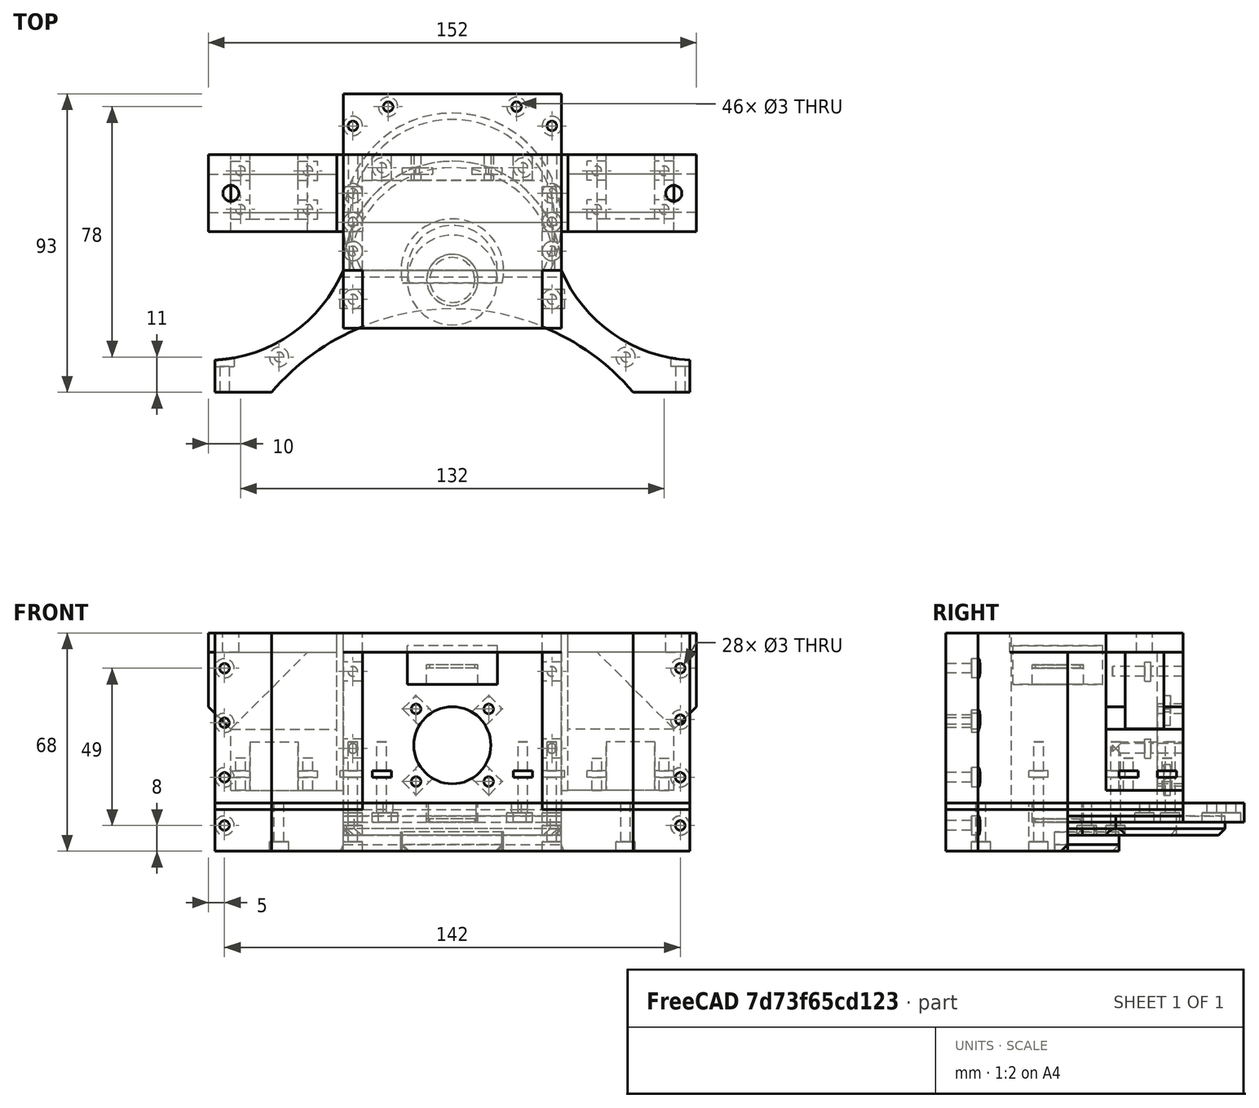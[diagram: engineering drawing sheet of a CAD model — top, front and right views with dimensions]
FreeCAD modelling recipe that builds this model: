
FCSTD DOCUMENT  (FreeCAD 0.19R24291 (Git))
Label: bazovina-part-J_rear-gearbox-cover_013
License: All rights reserved
LicenseURL: http://en.wikipedia.org/wiki/All_rights_reserved
objects: Part::Cylinder×179, Part::Cut×89, Part::Compound×79, Part::Box×59, Part::Chamfer×18, Mesh::Feature×2, Part::FeaturePython×2, Part::Mirroring×1
note: 427 computed .brp shape members not serialized (recipe doc carries the construction recipe); baked Part::Feature solids carry a one-line shape summary decoded from their .brp

FEATURE [Part::Cylinder] Cylinder483  label="Válec483"
  Angle = 360
  AttacherType = Attacher::AttachEngine3D
  Height = 36
  Placement = pos=(-76.3,104,16) rot=(0,0,1;0rad)
  Radius = 46
FEATURE [Part::Cylinder] Cylinder484  label="Válec484"
  Angle = 360
  AttacherType = Attacher::AttachEngine3D
  Height = 36
  Placement = pos=(76.3,104,16) rot=(0,0,1;0rad)
  Radius = 46
FEATURE [Part::Box] Box177  label="Krychle177"
  AttacherType = Attacher::AttachEngine3D
  Height = 15
  Length = 148
  Placement = pos=(-74,48,16) rot=(0,0,1;0rad)
  Width = 38
FEATURE [Part::Cut] Cut186
  Base = -> Box177
  Tool = -> Cylinder483
FEATURE [Part::Cut] Cut187
  Base = -> Cut186
  Tool = -> Cylinder484
FEATURE [Part::Cylinder] Cylinder486  label="Válec486"
  Angle = 360
  AttacherType = Attacher::AttachEngine3D
  Height = 15
  Placement = pos=(0,0,16) rot=(0,0,1;0rad)
  Radius = 74
FEATURE [Part::Cut] Cut189
  Base = -> Cut187
  Tool = -> Cylinder486
FEATURE [Part::Cylinder] Cylinder488  label="Válec488"
  Angle = 360
  AttacherType = Attacher::AttachEngine3D
  Height = 6
  Placement = pos=(0,86,21) rot=(0,0,1;0rad)
  Radius = 34
FEATURE [Part::Box] Box183  label="Krychle183"
  AttacherType = Attacher::AttachEngine3D
  Height = 40
  Length = 148
  Placement = pos=(-74,46,16) rot=(0,0,1;0rad)
  Width = 40
FEATURE [Part::Cut] Cut194
  Base = -> Cylinder488
  Tool = -> Box183
FEATURE [Part::Cylinder] Cylinder539  label="Válec539"
  Angle = 360
  AttacherType = Attacher::AttachEngine3D
  Height = 50
  Placement = pos=(71,80,24) rot=(1,0,0;1.5708rad)
  Radius = 1.5
FEATURE [Part::Cylinder] Cylinder540  label="Válec540"
  Angle = 360
  AttacherType = Attacher::AttachEngine3D
  Height = 50
  Placement = pos=(-71,80,24) rot=(1,0,0;1.5708rad)
  Radius = 1.5
FEATURE [Part::Compound] Compound348
  Links = -> [Cylinder539,Cylinder540]
FEATURE [Part::Cut] Cut209
  Base = -> Cut189
  Tool = -> Compound348
FEATURE [Part::Cylinder] Cylinder541  label="Válec541"
  Angle = 360
  AttacherType = Attacher::AttachEngine3D
  Height = 50
  Placement = pos=(-71,106,24) rot=(1,0,0;1.5708rad)
  Radius = 3
FEATURE [Part::Cylinder] Cylinder542  label="Válec542"
  Angle = 360
  AttacherType = Attacher::AttachEngine3D
  Height = 50
  Placement = pos=(71,106,24) rot=(1,0,0;1.5708rad)
  Radius = 3
FEATURE [Part::Compound] Compound349
  Links = -> [Cylinder542,Cylinder541]
FEATURE [Part::Cut] Cut210
  Base = -> Cut209
  Tool = -> Compound349
FEATURE [Part::Cylinder] Cylinder626  label="Válec626"
  Angle = 360
  AttacherType = Attacher::AttachEngine3D
  Height = 50
  Placement = pos=(-31,110,0) rot=(0,0,1;0.785398rad)
  Radius = 1.5
FEATURE [Part::Box] Box242  label="Krychle242"
  AttacherType = Attacher::AttachEngine3D
  Height = 4
  Length = 68
  Placement = pos=(-34,86,27) rot=(0,0,1;0rad)
  Width = 36
FEATURE [Part::Cylinder] Cylinder625  label="Válec625"
  Angle = 360
  AttacherType = Attacher::AttachEngine3D
  Height = 6
  Placement = pos=(0,86,16) rot=(0,0,1;0rad)
  Radius = 16
FEATURE [Part::Box] Box243  label="Krychle243"
  AttacherType = Attacher::AttachEngine3D
  Height = 40
  Length = 148
  Placement = pos=(-74,42,16) rot=(0,0,1;0rad)
  Width = 40
FEATURE [Part::Cut] Cut246
  Base = -> Cylinder625
  Tool = -> Box243
FEATURE [Part::Cylinder] Cylinder632  label="Válec632"
  Angle = 360
  AttacherType = Attacher::AttachEngine3D
  Height = 3
  Placement = pos=(31,110,0) rot=(0,0,1;0.785398rad)
  Radius = 3
FEATURE [Part::Cylinder] Cylinder633  label="Válec633"
  Angle = 360
  AttacherType = Attacher::AttachEngine3D
  Height = 3
  Placement = pos=(31,92,21) rot=(0,0,1;0.785398rad)
  Radius = 3
FEATURE [Part::Cylinder] Cylinder637  label="Válec637"
  Angle = 360
  AttacherType = Attacher::AttachEngine3D
  Height = 50
  Placement = pos=(-31,92,0) rot=(0,0,1;0.785398rad)
  Radius = 1.5
FEATURE [Part::Cylinder] Cylinder636  label="Válec636"
  Angle = 360
  AttacherType = Attacher::AttachEngine3D
  Height = 50
  Placement = pos=(31,110,0) rot=(0,0,1;0.785398rad)
  Radius = 1.5
FEATURE [Part::Cylinder] Cylinder634  label="Válec634"
  Angle = 360
  AttacherType = Attacher::AttachEngine3D
  Height = 50
  Placement = pos=(-31,110,0) rot=(0,0,1;0.785398rad)
  Radius = 1.5
FEATURE [Part::Cylinder] Cylinder631  label="Válec631"
  Angle = 360
  AttacherType = Attacher::AttachEngine3D
  Height = 3
  Placement = pos=(-31,92,21) rot=(0,0,1;0.785398rad)
  Radius = 3
FEATURE [Part::Cylinder] Cylinder640  label="Válec640"
  Angle = 360
  AttacherType = Attacher::AttachEngine3D
  Height = 6
  Placement = pos=(0,83,25) rot=(0,0,1;0rad)
  Radius = 8
FEATURE [Part::Cylinder] Cylinder638  label="Válec638"
  Angle = 360
  AttacherType = Attacher::AttachEngine3D
  Height = 6
  Placement = pos=(0,83,25) rot=(0,0,1;0rad)
  Radius = 8
FEATURE [Part::Cylinder] Cylinder629  label="Válec629"
  Angle = 360
  AttacherType = Attacher::AttachEngine3D
  Height = 50
  Placement = pos=(31,92,0) rot=(0,0,1;0.785398rad)
  Radius = 1.5
FEATURE [Part::Cylinder] Cylinder630  label="Válec630"
  Angle = 360
  AttacherType = Attacher::AttachEngine3D
  Height = 3
  Placement = pos=(-31,110,0) rot=(0,0,1;0.785398rad)
  Radius = 3
FEATURE [Part::Cylinder] Cylinder628  label="Válec628"
  Angle = 360
  AttacherType = Attacher::AttachEngine3D
  Height = 50
  Placement = pos=(31,110,0) rot=(0,0,1;0.785398rad)
  Radius = 1.5
FEATURE [Part::Cylinder] Cylinder627  label="Válec627"
  Angle = 360
  AttacherType = Attacher::AttachEngine3D
  Height = 50
  Placement = pos=(-31,92,0) rot=(0,0,1;0.785398rad)
  Radius = 1.5
FEATURE [Part::Compound] Compound385
  Links = -> [Cylinder626,Cylinder627,Cylinder628,Cylinder629]
FEATURE [Part::Cut] Cut248
  Base = -> Cut194
  Tool = -> Compound385
FEATURE [Part::Cylinder] Cylinder635  label="Válec635"
  Angle = 360
  AttacherType = Attacher::AttachEngine3D
  Height = 50
  Placement = pos=(31,92,0) rot=(0,0,1;0.785398rad)
  Radius = 1.5
FEATURE [Part::Cylinder] Cylinder639  label="Válec639"
  Angle = 360
  AttacherType = Attacher::AttachEngine3D
  Height = 6
  Placement = pos=(0,83,25) rot=(0,0,1;0rad)
  Radius = 8
FEATURE [Part::Compound] Compound386
  Links = -> [Cylinder634,Cylinder637,Cylinder636,Cylinder635]
FEATURE [Part::Cut] Cut247
  Base = -> Box242
  Tool = -> Compound386
FEATURE [Part::Cut] Cut250
  Base = -> Cut247
  Tool = -> Cylinder638
FEATURE [Part::Cut] Cut252
  Base = -> Cut210
  Tool = -> Cylinder640
FEATURE [Part::Compound] Compound387
  Links = -> [Cylinder630,Cylinder631,Cylinder632,Cylinder633]
FEATURE [Part::Cut] Cut249
  Base = -> Cut248
  Tool = -> Compound387
FEATURE [Part::Cut] Cut251
  Base = -> Cut249
  Tool = -> Cylinder639
FEATURE [Part::Compound] Compound388  label="bazovina-part-J"
  Links = -> [Cut252,Cut250,Cut251,Cut246]
FEATURE [Part::Box] Box244  label="Krychle244"
  AttacherType = Attacher::AttachEngine3D
  Height = 40
  Length = 148
  Placement = pos=(-74,46,16) rot=(0,0,1;0rad)
  Width = 40
FEATURE [Part::Cylinder] Cylinder641  label="Válec641"
  Angle = 360
  AttacherType = Attacher::AttachEngine3D
  Height = 3
  Placement = pos=(31,92,21) rot=(0,0,1;0.785398rad)
  Radius = 3
FEATURE [Part::Cylinder] Cylinder642  label="Válec642"
  Angle = 360
  AttacherType = Attacher::AttachEngine3D
  Height = 36
  Placement = pos=(-76.3,104,16) rot=(0,0,1;0rad)
  Radius = 46
FEATURE [Part::Cylinder] Cylinder643  label="Válec643"
  Angle = 360
  AttacherType = Attacher::AttachEngine3D
  Height = 36
  Placement = pos=(76.3,104,16) rot=(0,0,1;0rad)
  Radius = 46
FEATURE [Part::Box] Box245  label="Krychle245"
  AttacherType = Attacher::AttachEngine3D
  Height = 15
  Length = 148
  Placement = pos=(-74,48,16) rot=(0,0,1;0rad)
  Width = 38
FEATURE [Part::Cylinder] Cylinder644  label="Válec644"
  Angle = 360
  AttacherType = Attacher::AttachEngine3D
  Height = 50
  Placement = pos=(-71,80,24) rot=(1,0,0;1.5708rad)
  Radius = 1.5
FEATURE [Part::Cylinder] Cylinder645  label="Válec645"
  Angle = 360
  AttacherType = Attacher::AttachEngine3D
  Height = 50
  Placement = pos=(-31,110,0) rot=(0,0,1;0.785398rad)
  Radius = 1.5
FEATURE [Part::Cylinder] Cylinder646  label="Válec646"
  Angle = 360
  AttacherType = Attacher::AttachEngine3D
  Height = 15
  Placement = pos=(0,0,16) rot=(0,0,1;0rad)
  Radius = 74
FEATURE [Part::Cylinder] Cylinder647  label="Válec647"
  Angle = 360
  AttacherType = Attacher::AttachEngine3D
  Height = 6
  Placement = pos=(0,86,21) rot=(0,0,1;0rad)
  Radius = 34
FEATURE [Part::Cylinder] Cylinder648  label="Válec648"
  Angle = 360
  AttacherType = Attacher::AttachEngine3D
  Height = 50
  Placement = pos=(-71,106,24) rot=(1,0,0;1.5708rad)
  Radius = 3
FEATURE [Part::Box] Box246  label="Krychle246"
  AttacherType = Attacher::AttachEngine3D
  Height = 4
  Length = 68
  Placement = pos=(-34,86,27) rot=(0,0,1;0rad)
  Width = 36
FEATURE [Part::Box] Box247  label="Krychle247"
  AttacherType = Attacher::AttachEngine3D
  Height = 40
  Length = 148
  Placement = pos=(-74,42,16) rot=(0,0,1;0rad)
  Width = 40
FEATURE [Part::Cylinder] Cylinder649  label="Válec649"
  Angle = 360
  AttacherType = Attacher::AttachEngine3D
  Height = 50
  Placement = pos=(71,80,24) rot=(1,0,0;1.5708rad)
  Radius = 1.5
FEATURE [Part::Compound] Compound390
  Links = -> [Cylinder649,Cylinder644]
FEATURE [Part::Cylinder] Cylinder650  label="Válec650"
  Angle = 360
  AttacherType = Attacher::AttachEngine3D
  Height = 6
  Placement = pos=(0,86,16) rot=(0,0,1;0rad)
  Radius = 16
FEATURE [Part::Cylinder] Cylinder651  label="Válec651"
  Angle = 360
  AttacherType = Attacher::AttachEngine3D
  Height = 50
  Placement = pos=(71,106,24) rot=(1,0,0;1.5708rad)
  Radius = 3
FEATURE [Part::Compound] Compound391
  Links = -> [Cylinder651,Cylinder648]
FEATURE [Part::Cylinder] Cylinder652  label="Válec652"
  Angle = 360
  AttacherType = Attacher::AttachEngine3D
  Height = 3
  Placement = pos=(31,110,0) rot=(0,0,1;0.785398rad)
  Radius = 3
FEATURE [Part::Cylinder] Cylinder653  label="Válec653"
  Angle = 360
  AttacherType = Attacher::AttachEngine3D
  Height = 50
  Placement = pos=(31,110,0) rot=(0,0,1;0.785398rad)
  Radius = 1.5
FEATURE [Part::Cylinder] Cylinder654  label="Válec654"
  Angle = 360
  AttacherType = Attacher::AttachEngine3D
  Height = 50
  Placement = pos=(-31,110,0) rot=(0,0,1;0.785398rad)
  Radius = 1.5
FEATURE [Part::Cylinder] Cylinder655  label="Válec655"
  Angle = 360
  AttacherType = Attacher::AttachEngine3D
  Height = 3
  Placement = pos=(-31,92,21) rot=(0,0,1;0.785398rad)
  Radius = 3
FEATURE [Part::Cylinder] Cylinder656  label="Válec656"
  Angle = 360
  AttacherType = Attacher::AttachEngine3D
  Height = 50
  Placement = pos=(-31,92,0) rot=(0,0,1;0.785398rad)
  Radius = 1.5
FEATURE [Part::Cylinder] Cylinder657  label="Válec657"
  Angle = 360
  AttacherType = Attacher::AttachEngine3D
  Height = 6
  Placement = pos=(0,83,25) rot=(0,0,1;0rad)
  Radius = 8
FEATURE [Part::Cylinder] Cylinder658  label="Válec658"
  Angle = 360
  AttacherType = Attacher::AttachEngine3D
  Height = 50
  Placement = pos=(31,92,0) rot=(0,0,1;0.785398rad)
  Radius = 1.5
FEATURE [Part::Cylinder] Cylinder659  label="Válec659"
  Angle = 360
  AttacherType = Attacher::AttachEngine3D
  Height = 6
  Placement = pos=(0,83,25) rot=(0,0,1;0rad)
  Radius = 8
FEATURE [Part::Cylinder] Cylinder660  label="Válec660"
  Angle = 360
  AttacherType = Attacher::AttachEngine3D
  Height = 3
  Placement = pos=(-31,110,0) rot=(0,0,1;0.785398rad)
  Radius = 3
FEATURE [Part::Compound] Compound394
  Links = -> [Cylinder660,Cylinder655,Cylinder652,Cylinder641]
FEATURE [Part::Cylinder] Cylinder661  label="Válec661"
  Angle = 360
  AttacherType = Attacher::AttachEngine3D
  Height = 50
  Placement = pos=(31,110,0) rot=(0,0,1;0.785398rad)
  Radius = 1.5
FEATURE [Part::Cylinder] Cylinder662  label="Válec662"
  Angle = 360
  AttacherType = Attacher::AttachEngine3D
  Height = 50
  Placement = pos=(-31,92,0) rot=(0,0,1;0.785398rad)
  Radius = 1.5
FEATURE [Part::Compound] Compound392
  Links = -> [Cylinder645,Cylinder662,Cylinder661,Cylinder658]
FEATURE [Part::Cylinder] Cylinder663  label="Válec663"
  Angle = 360
  AttacherType = Attacher::AttachEngine3D
  Height = 6
  Placement = pos=(0,83,25) rot=(0,0,1;0rad)
  Radius = 8
FEATURE [Part::Cylinder] Cylinder664  label="Válec664"
  Angle = 360
  AttacherType = Attacher::AttachEngine3D
  Height = 50
  Placement = pos=(31,92,0) rot=(0,0,1;0.785398rad)
  Radius = 1.5
FEATURE [Part::Compound] Compound393
  Links = -> [Cylinder654,Cylinder656,Cylinder653,Cylinder664]
FEATURE [Part::Cut] Cut255
  Base = -> Box245
  Tool = -> Cylinder642
FEATURE [Part::Cut] Cut256
  Base = -> Cylinder647
  Tool = -> Box244
FEATURE [Part::Cut] Cut259
  Base = -> Box246
  Tool = -> Compound393
FEATURE [Part::Cut] Cut260
  Base = -> Cut259
  Tool = -> Cylinder659
FEATURE [Part::Cut] Cut262
  Base = -> Cylinder650
  Tool = -> Box247
FEATURE [Part::Cut] Cut263
  Base = -> Cut255
  Tool = -> Cylinder643
FEATURE [Part::Cut] Cut261
  Base = -> Cut263
  Tool = -> Cylinder646
FEATURE [Part::Cut] Cut253
  Base = -> Cut261
  Tool = -> Compound390
FEATURE [Part::Cut] Cut264
  Base = -> Cut253
  Tool = -> Compound391
FEATURE [Part::Cut] Cut254
  Base = -> Cut264
  Tool = -> Cylinder657
FEATURE [Part::Cut] Cut265
  Base = -> Cut256
  Tool = -> Compound392
FEATURE [Part::Cut] Cut258
  Base = -> Cut265
  Tool = -> Compound394
FEATURE [Part::Cut] Cut257
  Base = -> Cut258
  Tool = -> Cylinder663
FEATURE [Part::Compound] Compound389  label="bazovina-part-J001"
  Links = -> [Cut254,Cut260,Cut257,Cut262]
FEATURE [Part::Chamfer] Chamfer
  Base = -> Compound389
  Edges = 1 edges r=2: [Edge24]
FEATURE [Part::Chamfer] Chamfer001
  Base = -> Chamfer
  Edges = 1 edges r=2: [Edge94]
FEATURE [Part::Chamfer] Chamfer002
  Base = -> Chamfer001
  Edges = 1 edges r=2: [Edge4]
FEATURE [Part::Chamfer] Chamfer003  label="bazovina-part-J_fino"
  Base = -> Chamfer002
  Edges = 1 edges r=2: [Edge6]
FEATURE [Part::Chamfer] Chamfer004  label="bazovina-part-J_fino001"
  Base = -> Chamfer003
  Edges = 1 edges r=2: [Edge136]
FEATURE [Mesh::Feature] Mesh  label="bazovina-part-J_fino001 (Meshed)"
FEATURE [Part::FeaturePython] Tube032  # WARN: FeaturePython — macro-defined, semantics opaque (R4)
  AttacherType = Attacher::AttachEngine3D
  Height = 1
  InnerRadius = 7
  OuterRadius = 8
  Placement = pos=(0,83,25) rot=(0,0,1;0rad)
FEATURE [Part::Cylinder] Cylinder665  label="Válec665"
  Angle = 360
  AttacherType = Attacher::AttachEngine3D
  Height = 36
  Placement = pos=(76.3,104,16) rot=(0,0,1;0rad)
  Radius = 46
FEATURE [Part::Cylinder] Cylinder666  label="Válec666"
  Angle = 360
  AttacherType = Attacher::AttachEngine3D
  Height = 36
  Placement = pos=(-76.3,104,16) rot=(0,0,1;0rad)
  Radius = 46
FEATURE [Part::Box] Box248  label="Krychle248"
  AttacherType = Attacher::AttachEngine3D
  Height = 15
  Length = 148
  Placement = pos=(-74,48,16) rot=(0,0,1;0rad)
  Width = 38
FEATURE [Part::Cut] Cut269
  Base = -> Box248
  Tool = -> Cylinder666
FEATURE [Part::Cut] Cut270
  Base = -> Cut269
  Tool = -> Cylinder665
FEATURE [Part::Cylinder] Cylinder667  label="Válec667"
  Angle = 360
  AttacherType = Attacher::AttachEngine3D
  Height = 15
  Placement = pos=(0,0,16) rot=(0,0,1;0rad)
  Radius = 74
FEATURE [Part::Cut] Cut267
  Base = -> Cut270
  Tool = -> Cylinder667
FEATURE [Part::Box] Box249  label="Krychle249"
  AttacherType = Attacher::AttachEngine3D
  Height = 6
  Length = 68
  Placement = pos=(-34,86,25) rot=(0,0,1;0rad)
  Width = 36
FEATURE [Part::Box] Box250  label="Krychle250"
  AttacherType = Attacher::AttachEngine3D
  Height = 40
  Length = 148
  Placement = pos=(-74,46,16) rot=(0,0,1;0rad)
  Width = 40
FEATURE [Part::Box] Box251  label="Krychle251"
  AttacherType = Attacher::AttachEngine3D
  Height = 40
  Length = 148
  Placement = pos=(-74,42,16) rot=(0,0,1;0rad)
  Width = 40
FEATURE [Part::Cylinder] Cylinder668  label="Válec668"
  Angle = 360
  AttacherType = Attacher::AttachEngine3D
  Height = 3
  Placement = pos=(31,110,0) rot=(0,0,1;0.785398rad)
  Radius = 3
FEATURE [Part::Cylinder] Cylinder669  label="Válec669"
  Angle = 360
  AttacherType = Attacher::AttachEngine3D
  Height = 50
  Placement = pos=(-31,92,0) rot=(0,0,1;0.785398rad)
  Radius = 1.5
FEATURE [Part::Cylinder] Cylinder670  label="Válec670"
  Angle = 360
  AttacherType = Attacher::AttachEngine3D
  Height = 50
  Placement = pos=(-71,80,24) rot=(1,0,0;1.5708rad)
  Radius = 1.5
FEATURE [Part::Cylinder] Cylinder671  label="Válec671"
  Angle = 360
  AttacherType = Attacher::AttachEngine3D
  Height = 6
  Placement = pos=(0,86,21) rot=(0,0,1;0rad)
  Radius = 34
FEATURE [Part::Cylinder] Cylinder672  label="Válec672"
  Angle = 360
  AttacherType = Attacher::AttachEngine3D
  Height = 50
  Placement = pos=(31,110,0) rot=(0,0,1;0.785398rad)
  Radius = 1.5
FEATURE [Part::Cylinder] Cylinder673  label="Válec673"
  Angle = 360
  AttacherType = Attacher::AttachEngine3D
  Height = 50
  Placement = pos=(-31,110,0) rot=(0,0,1;0.785398rad)
  Radius = 1.5
FEATURE [Part::Cylinder] Cylinder674  label="Válec674"
  Angle = 360
  AttacherType = Attacher::AttachEngine3D
  Height = 6
  Placement = pos=(0,86,16) rot=(0,0,1;0rad)
  Radius = 16
FEATURE [Part::Cut] Cut268
  Base = -> Cylinder674
  Tool = -> Box251
FEATURE [Part::Cylinder] Cylinder675  label="Válec675"
  Angle = 360
  AttacherType = Attacher::AttachEngine3D
  Height = 50
  Placement = pos=(-31,110,0) rot=(0,0,1;0.785398rad)
  Radius = 1.5
FEATURE [Part::Cylinder] Cylinder676  label="Válec676"
  Angle = 360
  AttacherType = Attacher::AttachEngine3D
  Height = 3
  Placement = pos=(31,92,21) rot=(0,0,1;0.785398rad)
  Radius = 3
FEATURE [Part::Cylinder] Cylinder677  label="Válec677"
  Angle = 360
  AttacherType = Attacher::AttachEngine3D
  Height = 50
  Placement = pos=(-71,106,24) rot=(1,0,0;1.5708rad)
  Radius = 3
FEATURE [Part::Cylinder] Cylinder678  label="Válec678"
  Angle = 360
  AttacherType = Attacher::AttachEngine3D
  Height = 50
  Placement = pos=(71,106,24) rot=(1,0,0;1.5708rad)
  Radius = 3
FEATURE [Part::Compound] Compound398
  Links = -> [Cylinder678,Cylinder677]
FEATURE [Part::Cylinder] Cylinder679  label="Válec679"
  Angle = 360
  AttacherType = Attacher::AttachEngine3D
  Height = 50
  Placement = pos=(71,80,24) rot=(1,0,0;1.5708rad)
  Radius = 1.5
FEATURE [Part::Compound] Compound395
  Links = -> [Cylinder679,Cylinder670]
FEATURE [Part::Cut] Cut271
  Base = -> Cylinder671
  Tool = -> Box250
FEATURE [Part::Cut] Cut272
  Base = -> Cut267
  Tool = -> Compound395
FEATURE [Part::Cut] Cut273
  Base = -> Cut272
  Tool = -> Compound398
FEATURE [Part::Cylinder] Cylinder680  label="Válec680"
  Angle = 360
  AttacherType = Attacher::AttachEngine3D
  Height = 50
  Placement = pos=(31,92,0) rot=(0,0,1;0.785398rad)
  Radius = 1.5
FEATURE [Part::Compound] Compound397
  Links = -> [Cylinder673,Cylinder669,Cylinder672,Cylinder680]
FEATURE [Part::Cut] Cut276
  Base = -> Box249
  Tool = -> Compound397
FEATURE [Part::Cylinder] Cylinder681  label="Válec681"
  Angle = 360
  AttacherType = Attacher::AttachEngine3D
  Height = 50
  Placement = pos=(-31,92,0) rot=(0,0,1;0.785398rad)
  Radius = 1.5
FEATURE [Part::Cylinder] Cylinder682  label="Válec682"
  Angle = 360
  AttacherType = Attacher::AttachEngine3D
  Height = 6
  Placement = pos=(0,83,25) rot=(0,0,1;0rad)
  Radius = 8
FEATURE [Part::Cut] Cut266
  Base = -> Cut276
  Tool = -> Cylinder682
FEATURE [Part::Cylinder] Cylinder683  label="Válec683"
  Angle = 360
  AttacherType = Attacher::AttachEngine3D
  Height = 3
  Placement = pos=(-31,110,0) rot=(0,0,1;0.785398rad)
  Radius = 3
FEATURE [Part::Cylinder] Cylinder684  label="Válec684"
  Angle = 360
  AttacherType = Attacher::AttachEngine3D
  Height = 6
  Placement = pos=(0,83,25) rot=(0,0,1;0rad)
  Radius = 8
FEATURE [Part::Cylinder] Cylinder685  label="Válec685"
  Angle = 360
  AttacherType = Attacher::AttachEngine3D
  Height = 50
  Placement = pos=(31,92,0) rot=(0,0,1;0.785398rad)
  Radius = 1.5
FEATURE [Part::Cylinder] Cylinder686  label="Válec686"
  Angle = 360
  AttacherType = Attacher::AttachEngine3D
  Height = 50
  Placement = pos=(31,110,0) rot=(0,0,1;0.785398rad)
  Radius = 1.5
FEATURE [Part::Compound] Compound396
  Links = -> [Cylinder675,Cylinder681,Cylinder686,Cylinder685]
FEATURE [Part::Cut] Cut277
  Base = -> Cut271
  Tool = -> Compound396
FEATURE [Part::Cylinder] Cylinder687  label="Válec687"
  Angle = 360
  AttacherType = Attacher::AttachEngine3D
  Height = 6
  Placement = pos=(0,83,25) rot=(0,0,1;0rad)
  Radius = 8
FEATURE [Part::Cylinder] Cylinder688  label="Válec688"
  Angle = 360
  AttacherType = Attacher::AttachEngine3D
  Height = 3
  Placement = pos=(-31,92,21) rot=(0,0,1;0.785398rad)
  Radius = 3
FEATURE [Part::Compound] Compound400
  Links = -> [Cylinder683,Cylinder688,Cylinder668,Cylinder676]
FEATURE [Part::Cut] Cut275
  Base = -> Cut277
  Tool = -> Compound400
FEATURE [Part::Cut] Cut274
  Base = -> Cut275
  Tool = -> Cylinder687
FEATURE [Part::Cut] Cut278
  Base = -> Cut273
  Tool = -> Cylinder684
FEATURE [Part::Box] Box715  label="Krychle715"
  AttacherType = Attacher::AttachEngine3D
  Height = 6
  Length = 2
  Placement = pos=(34,110,69) rot=(0,0,1;1.5708rad)
  Width = 6
FEATURE [Part::Cylinder] Cylinder1767  label="Válec1767"
  Angle = 360
  AttacherType = Attacher::AttachEngine3D
  Height = 50
  Placement = pos=(31,150,72) rot=(1,0,0;1.5708rad)
  Radius = 1.5
FEATURE [Part::Cylinder] Cylinder1764  label="Válec1764"
  Angle = 360
  AttacherType = Attacher::AttachEngine3D
  Height = 50
  Placement = pos=(-31,150,48) rot=(1,0,0;1.5708rad)
  Radius = 1.5
FEATURE [Part::Cylinder] Cylinder1765  label="Válec1765"
  Angle = 360
  AttacherType = Attacher::AttachEngine3D
  Height = 50
  Placement = pos=(-31,150,72) rot=(1,0,0;1.5708rad)
  Radius = 1.5
FEATURE [Part::Box] Box711  label="Krychle711"
  AttacherType = Attacher::AttachEngine3D
  Height = 2
  Length = 6
  Placement = pos=(-27,74,39) rot=(0,0,1;1.5708rad)
  Width = 8
FEATURE [Part::Box] Box712  label="Krychle712"
  AttacherType = Attacher::AttachEngine3D
  Height = 6
  Length = 2
  Placement = pos=(-28,110,45) rot=(0,0,1;1.5708rad)
  Width = 6
FEATURE [Part::Box] Box713  label="Krychle713"
  AttacherType = Attacher::AttachEngine3D
  Height = 6
  Length = 2
  Placement = pos=(-28,110,69) rot=(0,0,1;1.5708rad)
  Width = 6
FEATURE [Part::Box] Box714  label="Krychle714"
  AttacherType = Attacher::AttachEngine3D
  Height = 6
  Length = 2
  Placement = pos=(34,110,45) rot=(0,0,1;1.5708rad)
  Width = 6
FEATURE [Part::Cylinder] Cylinder1766  label="Válec1766"
  Angle = 360
  AttacherType = Attacher::AttachEngine3D
  Height = 50
  Placement = pos=(31,150,48) rot=(1,0,0;1.5708rad)
  Radius = 1.5
FEATURE [Part::Box] Box717  label="Krychle717"
  AttacherType = Attacher::AttachEngine3D
  Height = 2
  Length = 6
  Placement = pos=(-27,98,39) rot=(0,0,1;1.5708rad)
  Width = 8
FEATURE [Part::Cylinder] Cylinder1768  label="Válec1768"
  Angle = 360
  AttacherType = Attacher::AttachEngine3D
  Height = 50
  Placement = pos=(-31,101,0) rot=(0,0,1;0.785398rad)
  Radius = 1.5
FEATURE [Part::Box] Box718  label="Krychle718"
  AttacherType = Attacher::AttachEngine3D
  Height = 6
  Length = 8
  Placement = pos=(-19,116,46) rot=(0,0,1;0rad)
  Width = 2
FEATURE [Part::Box] Box719  label="Krychle719"
  AttacherType = Attacher::AttachEngine3D
  Height = 6
  Length = 49
  Placement = pos=(28,86,78) rot=(0,1,0;1.5708rad)
  Width = 36
FEATURE [Part::Box] Box721  label="Krychle721"
  AttacherType = Attacher::AttachEngine3D
  Height = 2
  Length = 6
  Placement = pos=(35,98,39) rot=(0,0,1;1.5708rad)
  Width = 8
FEATURE [Part::Cylinder] Cylinder1770  label="Válec1770"
  Angle = 360
  AttacherType = Attacher::AttachEngine3D
  Height = 50
  Placement = pos=(31,101,0) rot=(0,0,1;0.785398rad)
  Radius = 1.5
FEATURE [Part::Box] Box723  label="Krychle723"
  AttacherType = Attacher::AttachEngine3D
  Height = 6
  Length = 49
  Placement = pos=(-34,86,78) rot=(0,1,0;1.5708rad)
  Width = 36
FEATURE [Part::Box] Box722  label="Krychle722"
  AttacherType = Attacher::AttachEngine3D
  Height = 49
  Length = 56
  Placement = pos=(-28,114,29) rot=(0,0,1;0rad)
  Width = 8
FEATURE [Part::Box] Box724  label="Krychle724"
  AttacherType = Attacher::AttachEngine3D
  Height = 6
  Length = 8
  Placement = pos=(11,116,46) rot=(0,0,1;0rad)
  Width = 2
FEATURE [Part::Compound] Compound
  Links = -> [Box712,Box713,Box714,Box715]
FEATURE [Part::Compound] Compound890
  Links = -> [Cylinder1764,Cylinder1765,Cylinder1766,Cylinder1767]
FEATURE [Part::Compound] Compound893
  Links = -> [Box721]
FEATURE [Part::Compound] Compound897
  Links = -> [Box717]
FEATURE [Part::Cut] Cut522
  Base = -> Box723
  Tool = -> Compound897
FEATURE [Part::Compound] Compound896
  Links = -> [Cylinder1768]
FEATURE [Part::Compound] Compound892
  Links = -> [Cylinder1770]
FEATURE [Part::Cut] Cut524
  Base = -> Box719
  Tool = -> Compound892
FEATURE [Part::Cut] Cut525
  Base = -> Cut524
  Tool = -> Compound893
FEATURE [Part::Cylinder] Cylinder1773  label="Válec1773"
  Angle = 360
  AttacherType = Attacher::AttachEngine3D
  Height = 40
  Placement = pos=(-16,140,49) rot=(1,0,0;1.5708rad)
  Radius = 1.5
FEATURE [Part::Cylinder] Cylinder1784  label="Válec1784"
  Angle = 360
  AttacherType = Attacher::AttachEngine3D
  Height = 50
  Placement = pos=(-71,80,39) rot=(1,0,0;1.5708rad)
  Radius = 1.5
FEATURE [Part::Cylinder] Cylinder1774  label="Válec1774"
  Angle = 360
  AttacherType = Attacher::AttachEngine3D
  Height = 20
  Placement = pos=(0,124,49) rot=(1,0,0;1.5708rad)
  Radius = 12
FEATURE [Part::Cylinder] Cylinder1778  label="Válec1778"
  Angle = 360
  AttacherType = Attacher::AttachEngine3D
  Height = 55
  Placement = pos=(76.3,104,29) rot=(0,0,1;0rad)
  Radius = 46
FEATURE [Part::Box] Box725  label="Krychle725"
  AttacherType = Attacher::AttachEngine3D
  Height = 8
  Length = 6
  Placement = pos=(-3,116,30) rot=(0,0,1;0rad)
  Width = 2
FEATURE [Part::Box] Box726  label="Krychle726"
  AttacherType = Attacher::AttachEngine3D
  Height = 8
  Length = 6
  Placement = pos=(-3,116,60) rot=(0,0,1;0rad)
  Width = 2
FEATURE [Part::Compound] Compound895
  Links = -> [Box726,Box725,Box718,Box724]
  Placement = pos=(-34.6482,0,14.3518) rot=(0,1,0;0.785398rad)
FEATURE [Part::Cylinder] Cylinder1777  label="Válec1777"
  Angle = 360
  AttacherType = Attacher::AttachEngine3D
  Height = 55
  Placement = pos=(-76.3,104,29) rot=(0,0,1;0rad)
  Radius = 46
FEATURE [Part::Cylinder] Cylinder1772  label="Válec1772"
  Angle = 360
  AttacherType = Attacher::AttachEngine3D
  Height = 40
  Placement = pos=(16,140,49) rot=(1,0,0;1.5708rad)
  Radius = 1.5
FEATURE [Part::Box] Box727  label="Krychle727"
  AttacherType = Attacher::AttachEngine3D
  Height = 55
  Length = 148
  Placement = pos=(-74,48,29) rot=(0,0,1;0rad)
  Width = 38
FEATURE [Part::Cylinder] Cylinder1775  label="Válec1775"
  Angle = 360
  AttacherType = Attacher::AttachEngine3D
  Height = 40
  Placement = pos=(0,140,65) rot=(1,0,0;1.5708rad)
  Radius = 1.5
FEATURE [Part::Cylinder] Cylinder1779  label="Válec1779"
  Angle = 360
  AttacherType = Attacher::AttachEngine3D
  Height = 55
  Placement = pos=(0,0,29) rot=(0,0,1;0rad)
  Radius = 74
FEATURE [Part::Box] Box728  label="Krychle728"
  AttacherType = Attacher::AttachEngine3D
  Height = 55
  Length = 56
  Placement = pos=(-28,0,29) rot=(0,0,1;0rad)
  Width = 200
FEATURE [Part::Cylinder] Cylinder1781  label="Válec1781"
  Angle = 360
  AttacherType = Attacher::AttachEngine3D
  Height = 50
  Placement = pos=(-71,106,73) rot=(1,0,0;1.5708rad)
  Radius = 3
FEATURE [Part::Cylinder] Cylinder1776  label="Válec1776"
  Angle = 360
  AttacherType = Attacher::AttachEngine3D
  Height = 40
  Placement = pos=(0,140,33) rot=(1,0,0;1.5708rad)
  Radius = 1.5
FEATURE [Part::Compound] Compound891
  Links = -> [Cylinder1775,Cylinder1772,Cylinder1773,Cylinder1776]
  Placement = pos=(-34.6482,0,14.3518) rot=(0,1,0;0.785398rad)
FEATURE [Part::Cut] Cut523
  Base = -> Box722
  Tool = -> Compound891
FEATURE [Part::Cylinder] Cylinder1780  label="Válec1780"
  Angle = 360
  AttacherType = Attacher::AttachEngine3D
  Height = 50
  Placement = pos=(-71,80,73) rot=(1,0,0;1.5708rad)
  Radius = 1.5
FEATURE [Part::Cylinder] Cylinder1782  label="Válec1782"
  Angle = 360
  AttacherType = Attacher::AttachEngine3D
  Height = 50
  Placement = pos=(-71,106,39) rot=(1,0,0;1.5708rad)
  Radius = 3
FEATURE [Part::Cylinder] Cylinder1783  label="Válec1783"
  Angle = 360
  AttacherType = Attacher::AttachEngine3D
  Height = 50
  Placement = pos=(71,106,73) rot=(1,0,0;1.5708rad)
  Radius = 3
FEATURE [Part::Cylinder] Cylinder1796  label="Válec1796"
  Angle = 360
  AttacherType = Attacher::AttachEngine3D
  Height = 50
  Placement = pos=(-22,118,0) rot=(0,0,1;0.785398rad)
  Radius = 1.5
FEATURE [Part::Cylinder] Cylinder1787  label="Válec1787"
  Angle = 360
  AttacherType = Attacher::AttachEngine3D
  Height = 50
  Placement = pos=(71,80,73) rot=(1,0,0;1.5708rad)
  Radius = 1.5
FEATURE [Part::Cylinder] Cylinder1789  label="Válec1789"
  Angle = 360
  AttacherType = Attacher::AttachEngine3D
  Height = 50
  Placement = pos=(71,80,57) rot=(1,0,0;1.5708rad)
  Radius = 1.5
FEATURE [Part::Cylinder] Cylinder1791  label="Válec1791"
  Angle = 360
  AttacherType = Attacher::AttachEngine3D
  Height = 50
  Placement = pos=(-71,106,56) rot=(1,0,0;1.5708rad)
  Radius = 3
FEATURE [Part::Cylinder] Cylinder1786  label="Válec1786"
  Angle = 360
  AttacherType = Attacher::AttachEngine3D
  Height = 50
  Placement = pos=(71,80,39) rot=(1,0,0;1.5708rad)
  Radius = 1.5
FEATURE [Part::Box] Box729  label="Krychle729"
  AttacherType = Attacher::AttachEngine3D
  Height = 2
  Length = 6
  Placement = pos=(35,74,39) rot=(0,0,1;1.5708rad)
  Width = 8
FEATURE [Part::Compound] Compound901
  Links = -> [Box729,Box711]
FEATURE [Part::Cylinder] Cylinder1793  label="Válec1793"
  Angle = 360
  AttacherType = Attacher::AttachEngine3D
  Height = 6
  Placement = pos=(0,83,68) rot=(0,0,1;0rad)
  Radius = 8
FEATURE [Part::Cylinder] Cylinder1785  label="Válec1785"
  Angle = 360
  AttacherType = Attacher::AttachEngine3D
  Height = 50
  Placement = pos=(71,106,39) rot=(1,0,0;1.5708rad)
  Radius = 3
FEATURE [Part::Box] Box730  label="Krychle730"
  AttacherType = Attacher::AttachEngine3D
  Height = 6
  Length = 68
  Placement = pos=(-34,68,78) rot=(0,0,1;0rad)
  Width = 54
FEATURE [Part::Box] Box731  label="Krychle731"
  AttacherType = Attacher::AttachEngine3D
  Height = 2
  Length = 8
  Placement = pos=(25,114,39) rot=(0,0,1;1.5708rad)
  Width = 6
FEATURE [Part::Cylinder] Cylinder1797  label="Válec1797"
  Angle = 360
  AttacherType = Attacher::AttachEngine3D
  Height = 50
  Placement = pos=(22,118,0) rot=(0,0,1;0.785398rad)
  Radius = 1.5
FEATURE [Part::Compound] Compound903
  Links = -> [Cylinder1796,Cylinder1797]
FEATURE [Part::Cylinder] Cylinder1788  label="Válec1788"
  Angle = 360
  AttacherType = Attacher::AttachEngine3D
  Height = 50
  Placement = pos=(-71,80,56) rot=(1,0,0;1.5708rad)
  Radius = 1.5
FEATURE [Part::Compound] Compound899
  Links = -> [Cylinder1784,Cylinder1786,Cylinder1780,Cylinder1787,Cylinder1788,Cylinder1789]
FEATURE [Part::Cylinder] Cylinder1790  label="Válec1790"
  Angle = 360
  AttacherType = Attacher::AttachEngine3D
  Height = 50
  Placement = pos=(71,106,57) rot=(1,0,0;1.5708rad)
  Radius = 3
FEATURE [Part::Compound] Compound898
  Links = -> [Cylinder1782,Cylinder1785,Cylinder1781,Cylinder1783,Cylinder1790,Cylinder1791]
FEATURE [Part::Cylinder] Cylinder1794  label="Válec1794"
  Angle = 360
  AttacherType = Attacher::AttachEngine3D
  Height = 50
  Placement = pos=(31,77,0) rot=(0,0,1;0.785398rad)
  Radius = 1.5
FEATURE [Part::Cylinder] Cylinder1792  label="Válec1792"
  Angle = 360
  AttacherType = Attacher::AttachEngine3D
  Height = 12
  Placement = pos=(0,83,68) rot=(0,0,1;0rad)
  Radius = 14
FEATURE [Part::Cylinder] Cylinder1795  label="Válec1795"
  Angle = 360
  AttacherType = Attacher::AttachEngine3D
  Height = 50
  Placement = pos=(-31,77,0) rot=(0,0,1;0.785398rad)
  Radius = 1.5
FEATURE [Part::Compound] Compound902
  Links = -> [Cylinder1794,Cylinder1795]
FEATURE [Part::Cut] Cut526
  Base = -> Cut522
  Tool = -> Compound896
FEATURE [Part::Cut] Cut537
  Base = -> Cylinder1792
  Tool = -> Cylinder1793
FEATURE [Part::Cut] Cut528
  Base = -> Cut523
  Tool = -> Cylinder1774
FEATURE [Part::Cut] Cut527
  Base = -> Cut528
  Tool = -> Compound895
FEATURE [Part::Compound] Compound894
  Links = -> [Cut527,Cut526,Cut525]
FEATURE [Part::Cut] Cut529
  Base = -> Compound894
  Tool = -> Compound890
FEATURE [Part::Cut] Cut530
  Base = -> Cut529
  Tool = -> Compound
FEATURE [Part::Cut] Cut536
  Base = -> Box727
  Tool = -> Cylinder1777
FEATURE [Part::Cut] Cut531
  Base = -> Cut536
  Tool = -> Cylinder1778
FEATURE [Part::Cut] Cut534
  Base = -> Cut531
  Tool = -> Box728
FEATURE [Part::Cut] Cut540
  Base = -> Cut530
  Tool = -> Compound903
FEATURE [Part::Cut] Cut535
  Base = -> Cut534
  Tool = -> Cylinder1779
FEATURE [Part::Cut] Cut532
  Base = -> Cut535
  Tool = -> Compound899
FEATURE [Part::Cut] Cut533
  Base = -> Cut532
  Tool = -> Compound898
FEATURE [Part::Cut] Cut538
  Base = -> Cut533
  Tool = -> Compound901
FEATURE [Part::Cut] Cut539
  Base = -> Cut538
  Tool = -> Compound902
FEATURE [Part::FeaturePython] Tube039  # WARN: FeaturePython — macro-defined, semantics opaque (R4)
  AttacherType = Attacher::AttachEngine3D
  Height = 1
  InnerRadius = 7
  OuterRadius = 8
  Placement = pos=(0,83,73) rot=(0,0,1;0rad)
FEATURE [Part::Compound] Compound900
  Links = -> [Cut537,Tube039]
FEATURE [Part::Cylinder] Cylinder1800  label="Válec1800"
  Angle = 360
  AttacherType = Attacher::AttachEngine3D
  Height = 16
  Placement = pos=(-64,117,25) rot=(0,0,1;0rad)
  Radius = 1.5
FEATURE [Part::Box] Box732  label="Krychle732"
  AttacherType = Attacher::AttachEngine3D
  Height = 2
  Length = 8
  Placement = pos=(-19,114,39) rot=(0,0,1;1.5708rad)
  Width = 6
FEATURE [Part::Compound] Compound904
  Links = -> [Box731,Box732]
FEATURE [Part::Cut] Cut541
  Base = -> Cut540
  Tool = -> Compound904
FEATURE [Part::Compound] Compound905  label="Base_rear-gearbox"
  Links = -> [Compound900,Cut539,Box730,Cut541]
FEATURE [Part::Cylinder] Cylinder1803  label="Válec1803"
  Angle = 360
  AttacherType = Attacher::AttachEngine3D
  Height = 16
  Placement = pos=(-64,105,25) rot=(0,0,1;0rad)
  Radius = 1.5
FEATURE [Part::Box] Box737  label="Krychle737"
  AttacherType = Attacher::AttachEngine3D
  Height = 15
  Length = 15
  Placement = pos=(-61,102,41) rot=(0,0,1;0rad)
  Width = 80
FEATURE [Part::Cylinder] Cylinder1802  label="Válec1802"
  Angle = 360
  AttacherType = Attacher::AttachEngine3D
  Height = 16
  Placement = pos=(-43,105,25) rot=(0,0,1;0rad)
  Radius = 1.5
FEATURE [Part::Box] Box733  label="Krychle733"
  AttacherType = Attacher::AttachEngine3D
  Height = 2
  Length = 6
  Placement = pos=(-67,102,35) rot=(0,0,1;0rad)
  Width = 6
FEATURE [Part::Cylinder] Cylinder1798  label="Válec1798"
  Angle = 360
  AttacherType = Attacher::AttachEngine3D
  Height = 20
  Placement = pos=(-84,-12,66) rot=(0,0,1;0rad)
  Radius = 2.5
FEATURE [Part::Cylinder] Cylinder1799  label="Válec1799"
  Angle = 360
  AttacherType = Attacher::AttachEngine3D
  Height = 16
  Placement = pos=(-43,117,25) rot=(0,0,1;0rad)
  Radius = 1.5
FEATURE [Part::Box] Box736  label="Krychle736"
  AttacherType = Attacher::AttachEngine3D
  Height = 24
  Length = 33
  Placement = pos=(-67,98,50) rot=(0,0,1;0rad)
  Width = 24
FEATURE [Part::Box] Box734  label="Krychle734"
  AttacherType = Attacher::AttachEngine3D
  Height = 2
  Length = 6
  Placement = pos=(-46,102,35) rot=(0,0,1;0rad)
  Width = 6
FEATURE [Part::Box] Box738  label="Krychle738"
  AttacherType = Attacher::AttachEngine3D
  Height = 24
  Length = 40
  Placement = pos=(-74,116,50) rot=(0,0,1;0rad)
  Width = 6
FEATURE [Part::Box] Box739  label="Krychle739"
  AttacherType = Attacher::AttachEngine3D
  Height = 6
  Length = 40
  Placement = pos=(-101,-24,76) rot=(0,0,1;0rad)
  Width = 24
FEATURE [Part::Box] Box735  label="Krychle735"
  AttacherType = Attacher::AttachEngine3D
  Height = 15
  Length = 15
  Placement = pos=(-61,102,41) rot=(0,0,1;0rad)
  Width = 80
FEATURE [Part::Box] Box740  label="Krychle740"
  AttacherType = Attacher::AttachEngine3D
  Height = 19
  Length = 33
  Placement = pos=(-67,98,41) rot=(0,0,1;0rad)
  Width = 24
FEATURE [Part::Cut] Cut543
  Base = -> Box740
  Placement = pos=(0,0,-10) rot=(0,0,1;0rad)
  Tool = -> Box737
FEATURE [Part::Box] Box741  label="Krychle741"
  AttacherType = Attacher::AttachEngine3D
  Height = 24
  Length = 40
  Placement = pos=(-74,98,50) rot=(0,0,1;0rad)
  Width = 6
FEATURE [Part::Box] Box742  label="Krychle742"
  AttacherType = Attacher::AttachEngine3D
  Height = 2
  Length = 6
  Placement = pos=(-67,114,35) rot=(0,0,1;0rad)
  Width = 6
FEATURE [Part::Cylinder] Cylinder1801  label="Válec1801"
  Angle = 360
  AttacherType = Attacher::AttachEngine3D
  Height = 20
  Placement = pos=(-102,-16,66) rot=(0,0,1;0rad)
  Radius = 2.5
FEATURE [Part::Box] Box487  label="Krychle487"
  AttacherType = Attacher::AttachEngine3D
  Height = 2
  Length = 6
  Placement = pos=(-46,114,35) rot=(0,0,1;0rad)
  Width = 6
FEATURE [Part::Box] Box749  label="Krychle749"
  AttacherType = Attacher::AttachEngine3D
  Height = 2
  Length = 6
  Placement = pos=(-67,102,35) rot=(0,0,1;0rad)
  Width = 6
FEATURE [Part::Cylinder] Cylinder1807  label="Válec1807"
  Angle = 360
  AttacherType = Attacher::AttachEngine3D
  Height = 16
  Placement = pos=(-43,117,25) rot=(0,0,1;0rad)
  Radius = 1.5
FEATURE [Part::Box] Box750  label="Krychle750"
  AttacherType = Attacher::AttachEngine3D
  Height = 2
  Length = 6
  Placement = pos=(-46,102,35) rot=(0,0,1;0rad)
  Width = 6
FEATURE [Part::Box] Box748  label="Krychle748"
  AttacherType = Attacher::AttachEngine3D
  Height = 24
  Length = 33
  Placement = pos=(-67,98,50) rot=(0,0,1;0rad)
  Width = 24
FEATURE [Part::Box] Box743  label="Krychle743"
  AttacherType = Attacher::AttachEngine3D
  Height = 2
  Length = 6
  Placement = pos=(-46,114,35) rot=(0,0,1;0rad)
  Width = 6
FEATURE [Part::Box] Box751  label="Krychle751"
  AttacherType = Attacher::AttachEngine3D
  Height = 6
  Length = 40
  Placement = pos=(-101,-24,76) rot=(0,0,1;0rad)
  Width = 24
FEATURE [Part::Box] Box745  label="Krychle745"
  AttacherType = Attacher::AttachEngine3D
  Height = 2
  Length = 6
  Placement = pos=(-67,114,35) rot=(0,0,1;0rad)
  Width = 6
FEATURE [Part::Cylinder] Cylinder1805  label="Válec1805"
  Angle = 360
  AttacherType = Attacher::AttachEngine3D
  Height = 20
  Placement = pos=(-84,-12,66) rot=(0,0,1;0rad)
  Radius = 2.5
FEATURE [Part::Cylinder] Cylinder1806  label="Válec1806"
  Angle = 360
  AttacherType = Attacher::AttachEngine3D
  Height = 16
  Placement = pos=(-43,105,25) rot=(0,0,1;0rad)
  Radius = 1.5
FEATURE [Part::Cylinder] Cylinder1809  label="Válec1809"
  Angle = 360
  AttacherType = Attacher::AttachEngine3D
  Height = 16
  Placement = pos=(-64,117,25) rot=(0,0,1;0rad)
  Radius = 1.5
FEATURE [Part::Box] Box746  label="Krychle746"
  AttacherType = Attacher::AttachEngine3D
  Height = 24
  Length = 40
  Placement = pos=(-74,98,50) rot=(0,0,1;0rad)
  Width = 6
FEATURE [Part::Box] Box744  label="Krychle744"
  AttacherType = Attacher::AttachEngine3D
  Height = 24
  Length = 40
  Placement = pos=(-74,116,50) rot=(0,0,1;0rad)
  Width = 6
FEATURE [Part::Cylinder] Cylinder1808  label="Válec1808"
  Angle = 360
  AttacherType = Attacher::AttachEngine3D
  Height = 16
  Placement = pos=(-64,105,25) rot=(0,0,1;0rad)
  Radius = 1.5
FEATURE [Part::Cylinder] Cylinder1804  label="Válec1804"
  Angle = 360
  AttacherType = Attacher::AttachEngine3D
  Height = 20
  Placement = pos=(-102,-16,66) rot=(0,0,1;0rad)
  Radius = 2.5
FEATURE [Part::Box] Box747  label="Krychle747"
  AttacherType = Attacher::AttachEngine3D
  Height = 19
  Length = 33
  Placement = pos=(-67,98,41) rot=(0,0,1;0rad)
  Width = 24
FEATURE [Part::Compound] Compound526
  Links = -> [Cylinder1807,Cylinder1806,Cylinder1809,Cylinder1808]
FEATURE [Part::Compound] Compound524
  Links = -> [Cylinder1804,Cylinder1805]
  Placement = pos=(-10,0,0) rot=(0,0,1;0rad)
FEATURE [Part::Cut] Cut545
  Base = -> Box751
  Placement = pos=(27,122,-2) rot=(0,0,1;0rad)
  Tool = -> Compound524
FEATURE [Part::Chamfer] Chamfer059
  Base = -> Box748
  Edges = 1 edges r=23.9: [Edge2]
FEATURE [Part::Compound] Compound527
  Links = -> [Box749,Box745,Box750,Box743]
FEATURE [Part::Compound] Compound909
  Links = -> [Box733,Box742,Box734,Box487]
FEATURE [Part::Chamfer] Chamfer060
  Base = -> Box738
  Edges = 1 edges r=7: [Edge4]
FEATURE [Part::Compound] Compound908
  Links = -> [Cylinder1799,Cylinder1802,Cylinder1800,Cylinder1803]
FEATURE [Part::Cut] Cut544
  Base = -> Cut543
  Tool = -> Compound908
FEATURE [Part::Chamfer] Chamfer061
  Base = -> Box736
  Edges = 1 edges r=23.9: [Edge2]
FEATURE [Part::Chamfer] Chamfer062
  Base = -> Box744
  Edges = 1 edges r=7: [Edge4]
FEATURE [Part::Compound] Compound906
  Links = -> [Cylinder1801,Cylinder1798]
  Placement = pos=(-10,0,0) rot=(0,0,1;0rad)
FEATURE [Part::Cut] Cut542
  Base = -> Box739
  Placement = pos=(27,122,-2) rot=(0,0,1;0rad)
  Tool = -> Compound906
FEATURE [Part::Chamfer] Chamfer058
  Base = -> Box741
  Edges = 1 edges r=7: [Edge4]
FEATURE [Part::Chamfer] Chamfer005
  Base = -> Box746
  Edges = 1 edges r=7: [Edge4]
FEATURE [Part::Cut] Cut549
  Base = -> Cut544
  Tool = -> Compound909
FEATURE [Part::Compound] Compound910  label="stabilo_left_back"
  Links = -> [Chamfer058,Chamfer060,Chamfer061,Cut542,Cut549]
  Placement = pos=(-2,0,4) rot=(0,0,1;0rad)
FEATURE [Part::Cut] Cut547
  Base = -> Box747
  Placement = pos=(0,0,-10) rot=(0,0,1;0rad)
  Tool = -> Box735
FEATURE [Part::Cut] Cut546
  Base = -> Cut547
  Tool = -> Compound526
FEATURE [Part::Cut] Cut548
  Base = -> Cut546
  Tool = -> Compound527
FEATURE [Part::Compound] Compound907  label="stabilo_left_back001"
  Links = -> [Chamfer005,Chamfer062,Chamfer059,Cut545,Cut548]
FEATURE [Part::Mirroring] mirror004  label="stabilo_right_back"
  Base = (0,0,0)
  Normal = (1,0,0)
  Placement = pos=(2,0,4) rot=(0,0,1;0rad)
  Source = -> Compound907
FEATURE [Part::Box] Box  label="Krychle"
  AttacherType = Attacher::AttachEngine3D
  Height = 49
  Length = 2
  Placement = pos=(34,98,35) rot=(0,0,1;0rad)
  Width = 24
FEATURE [Part::Box] Box752  label="Krychle752"
  AttacherType = Attacher::AttachEngine3D
  Height = 49
  Length = 2
  Placement = pos=(-36,98,35) rot=(0,0,1;0rad)
  Width = 24
FEATURE [Part::Compound] Compound911  label="Base_rear-gearbox-stabil"
  Links = -> [Compound905,mirror004,Compound910,Box,Box752]
FEATURE [Part::Cylinder] Cylinder1810  label="Válec1810"
  Angle = 360
  AttacherType = Attacher::AttachEngine3D
  Height = 50
  Placement = pos=(-22,118,0) rot=(0,0,1;0.785398rad)
  Radius = 1.5
FEATURE [Part::Cylinder] Cylinder1811  label="Válec1811"
  Angle = 360
  AttacherType = Attacher::AttachEngine3D
  Height = 50
  Placement = pos=(22,118,0) rot=(0,0,1;0.785398rad)
  Radius = 1.5
FEATURE [Part::Compound] Compound912
  Links = -> [Cylinder1810,Cylinder1811]
FEATURE [Part::Cylinder] Cylinder1812  label="Válec1812"
  Angle = 360
  AttacherType = Attacher::AttachEngine3D
  Height = 3
  Placement = pos=(-22,118,0) rot=(0,0,1;0.785398rad)
  Radius = 3
FEATURE [Part::Cylinder] Cylinder1813  label="Válec1813"
  Angle = 360
  AttacherType = Attacher::AttachEngine3D
  Height = 3
  Placement = pos=(22,118,0) rot=(0,0,1;0.785398rad)
  Radius = 3
FEATURE [Part::Compound] Compound913
  Links = -> [Cylinder1812,Cylinder1813]
  Placement = pos=(0,0,25) rot=(0,0,1;0rad)
FEATURE [Part::Cylinder] Cylinder1814  label="Válec1814"
  Angle = 360
  AttacherType = Attacher::AttachEngine3D
  Height = 3
  Placement = pos=(-31,110,0) rot=(0,0,1;0.785398rad)
  Radius = 3
FEATURE [Part::Cylinder] Cylinder1815  label="Válec1815"
  Angle = 360
  AttacherType = Attacher::AttachEngine3D
  Height = 3
  Placement = pos=(31,110,0) rot=(0,0,1;0.785398rad)
  Radius = 3
FEATURE [Part::Compound] Compound914
  Links = -> [Cylinder1814,Cylinder1815]
  Placement = pos=(0,0,25) rot=(0,0,1;0rad)
FEATURE [Part::Cut] Cut
  Base = -> Cut266
  Tool = -> Compound912
FEATURE [Part::Cut] Cut550
  Base = -> Cut
  Tool = -> Compound914
FEATURE [Part::Cut] Cut551
  Base = -> Cut550
  Tool = -> Compound913
FEATURE [Part::Chamfer] Chamfer063
  Base = -> Cut278
  Edges = 1 edges r=2: [Edge24]
FEATURE [Part::Chamfer] Chamfer064
  Base = -> Cut268
  Edges = 1 edges r=2: [Edge7]
FEATURE [Part::Chamfer] Chamfer065
  Base = -> Cut274
  Edges = 3 edges r=2: [Edge3,Edge7,Edge11]
FEATURE [Part::Cylinder] Cylinder1891  label="Válec1891"
  Angle = 360
  AttacherType = Attacher::AttachEngine3D
  Height = 50
  Placement = pos=(-71,80,24) rot=(1,0,0;1.5708rad)
  Radius = 1.5
FEATURE [Part::Cylinder] Cylinder1894  label="Válec1894"
  Angle = 360
  AttacherType = Attacher::AttachEngine3D
  Height = 15
  Placement = pos=(0,0,16) rot=(0,0,1;0rad)
  Radius = 74
FEATURE [Part::Cylinder] Cylinder1897  label="Válec1897"
  Angle = 360
  AttacherType = Attacher::AttachEngine3D
  Height = 50
  Placement = pos=(-71,106,24) rot=(1,0,0;1.5708rad)
  Radius = 3
FEATURE [Part::Cylinder] Cylinder1895  label="Válec1895"
  Angle = 360
  AttacherType = Attacher::AttachEngine3D
  Height = 36
  Placement = pos=(-76.3,104,16) rot=(0,0,1;0rad)
  Radius = 46
FEATURE [Part::Cylinder] Cylinder1892  label="Válec1892"
  Angle = 360
  AttacherType = Attacher::AttachEngine3D
  Height = 36
  Placement = pos=(76.3,104,16) rot=(0,0,1;0rad)
  Radius = 46
FEATURE [Part::Cylinder] Cylinder1899  label="Válec1899"
  Angle = 360
  AttacherType = Attacher::AttachEngine3D
  Height = 50
  Placement = pos=(71,80,24) rot=(1,0,0;1.5708rad)
  Radius = 1.5
FEATURE [Part::Compound] Compound953
  Links = -> [Cylinder1899,Cylinder1891]
FEATURE [Part::Box] Box801  label="Krychle801"
  AttacherType = Attacher::AttachEngine3D
  Height = 15
  Length = 148
  Placement = pos=(-74,48,16) rot=(0,0,1;0rad)
  Width = 38
FEATURE [Part::Cut] Cut601
  Base = -> Box801
  Tool = -> Cylinder1895
FEATURE [Part::Cut] Cut602
  Base = -> Cut601
  Tool = -> Cylinder1892
FEATURE [Part::Cut] Cut608
  Base = -> Cut602
  Tool = -> Cylinder1894
FEATURE [Part::Cut] Cut607
  Base = -> Cut608
  Tool = -> Compound953
FEATURE [Part::Cylinder] Cylinder1898  label="Válec1898"
  Angle = 360
  AttacherType = Attacher::AttachEngine3D
  Height = 50
  Placement = pos=(71,106,24) rot=(1,0,0;1.5708rad)
  Radius = 3
FEATURE [Part::Compound] Compound955
  Links = -> [Cylinder1898,Cylinder1897]
FEATURE [Part::Cut] Cut605
  Base = -> Cut607
  Tool = -> Compound955
FEATURE [Part::Cylinder] Cylinder1902  label="Válec1902"
  Angle = 360
  AttacherType = Attacher::AttachEngine3D
  Height = 6
  Placement = pos=(0,83,25) rot=(0,0,1;0rad)
  Radius = 8
FEATURE [Part::Cut] Cut604
  Base = -> Cut605
  Tool = -> Cylinder1902
FEATURE [Part::Chamfer] Chamfer066
  Base = -> Cut604
  Edges = 1 edges r=2: [Edge24]
FEATURE [Part::Cylinder] Cylinder1920  label="Válec1920"
  Angle = 360
  AttacherType = Attacher::AttachEngine3D
  Height = 50
  Placement = pos=(-31,131,0) rot=(0,0,1;0.785398rad)
  Radius = 1.5
FEATURE [Part::Cylinder] Cylinder1924  label="Válec1924"
  Angle = 360
  AttacherType = Attacher::AttachEngine3D
  Height = 3
  Placement = pos=(54,59,0) rot=(0,0,1;0.785398rad)
  Radius = 3
FEATURE [Part::Cylinder] Cylinder1926  label="Válec1926"
  Angle = 360
  AttacherType = Attacher::AttachEngine3D
  Height = 6
  Placement = pos=(0,83,25) rot=(0,0,1;0rad)
  Radius = 8
FEATURE [Part::Cylinder] Cylinder1912  label="Válec1912"
  Angle = 360
  AttacherType = Attacher::AttachEngine3D
  Height = 50
  Placement = pos=(31,77,0) rot=(0,0,1;0.785398rad)
  Radius = 1.5
FEATURE [Part::Cylinder] Cylinder1921  label="Válec1921"
  Angle = 360
  AttacherType = Attacher::AttachEngine3D
  Height = 50
  Placement = pos=(31,131,0) rot=(0,0,1;0.785398rad)
  Radius = 1.5
FEATURE [Part::Compound] Compound964
  Links = -> [Cylinder1920,Cylinder1921]
FEATURE [Part::Cylinder] Cylinder1914  label="Válec1914"
  Angle = 360
  AttacherType = Attacher::AttachEngine3D
  Height = 50
  Placement = pos=(20,137,0) rot=(0,0,1;0.785398rad)
  Radius = 1.5
FEATURE [Part::Cylinder] Cylinder1915  label="Válec1915"
  Angle = 360
  AttacherType = Attacher::AttachEngine3D
  Height = 50
  Placement = pos=(-20,137,0) rot=(0,0,1;0.785398rad)
  Radius = 1.5
FEATURE [Part::Compound] Compound961
  Links = -> [Cylinder1915,Cylinder1914]
FEATURE [Part::Cylinder] Cylinder1913  label="Válec1913"
  Angle = 360
  AttacherType = Attacher::AttachEngine3D
  Height = 50
  Placement = pos=(-31,77,0) rot=(0,0,1;0.785398rad)
  Radius = 1.5
FEATURE [Part::Compound] Compound960
  Links = -> [Cylinder1912,Cylinder1913]
FEATURE [Part::Cylinder] Cylinder1922  label="Válec1922"
  Angle = 360
  AttacherType = Attacher::AttachEngine3D
  Height = 3
  Placement = pos=(31,77,0) rot=(0,0,1;0.785398rad)
  Radius = 3
FEATURE [Part::Cylinder] Cylinder1911  label="Válec1911"
  Angle = 360
  AttacherType = Attacher::AttachEngine3D
  Height = 50
  Placement = pos=(54,59,0) rot=(0,0,1;0.785398rad)
  Radius = 1.5
FEATURE [Part::Cylinder] Cylinder1910  label="Válec1910"
  Angle = 360
  AttacherType = Attacher::AttachEngine3D
  Height = 50
  Placement = pos=(-54,59,0) rot=(0,0,1;0.785398rad)
  Radius = 1.5
FEATURE [Part::Compound] Compound959
  Links = -> [Cylinder1911,Cylinder1910]
FEATURE [Part::Compound] Compound968
  Links = -> [Compound959,Compound960]
FEATURE [Part::Cylinder] Cylinder1923  label="Válec1923"
  Angle = 360
  AttacherType = Attacher::AttachEngine3D
  Height = 3
  Placement = pos=(-31,77,0) rot=(0,0,1;0.785398rad)
  Radius = 3
FEATURE [Part::Compound] Compound966
  Links = -> [Cylinder1922,Cylinder1923]
FEATURE [Part::Cylinder] Cylinder1925  label="Válec1925"
  Angle = 360
  AttacherType = Attacher::AttachEngine3D
  Height = 3
  Placement = pos=(-54,59,0) rot=(0,0,1;0.785398rad)
  Radius = 3
FEATURE [Part::Compound] Compound965
  Links = -> [Cylinder1924,Cylinder1925]
FEATURE [Part::Compound] Compound967
  Links = -> [Compound965,Compound966]
  Placement = pos=(0,0,16) rot=(0,0,1;0rad)
FEATURE [Part::Cut] Cut612
  Base = -> Chamfer066
  Tool = -> Compound967
FEATURE [Part::Cut] Cut613
  Base = -> Cut612
  Tool = -> Compound968
FEATURE [Part::Box] Box802  label="Krychle802"
  AttacherType = Attacher::AttachEngine3D
  Height = 6
  Length = 68
  Placement = pos=(-34,86,25) rot=(0,0,1;0rad)
  Width = 55
FEATURE [Part::Cut] Cut614
  Base = -> Box802
  Tool = -> Cylinder1926
FEATURE [Part::Cylinder] Cylinder1929  label="Válec1929"
  Angle = 360
  AttacherType = Attacher::AttachEngine3D
  Height = 50
  Placement = pos=(-31,101,0) rot=(0,0,1;0.785398rad)
  Radius = 1.5
FEATURE [Part::Cylinder] Cylinder1930  label="Válec1930"
  Angle = 360
  AttacherType = Attacher::AttachEngine3D
  Height = 50
  Placement = pos=(31,101,0) rot=(0,0,1;0.785398rad)
  Radius = 1.5
FEATURE [Part::Compound] Compound970
  Links = -> [Cylinder1929,Cylinder1930]
FEATURE [Part::Compound] Compound990
  Links = -> [Compound970,Compound961,Compound964]
FEATURE [Part::Cylinder] Cylinder1940  label="Válec1940"
  Angle = 360
  AttacherType = Attacher::AttachEngine3D
  Height = 3
  Placement = pos=(20,137,0) rot=(0,0,1;0.785398rad)
  Radius = 3
FEATURE [Part::Cylinder] Cylinder1937  label="Válec1937"
  Angle = 360
  AttacherType = Attacher::AttachEngine3D
  Height = 6
  Placement = pos=(0,83,25) rot=(0,0,1;0rad)
  Radius = 8
FEATURE [Part::Cylinder] Cylinder1941  label="Válec1941"
  Angle = 360
  AttacherType = Attacher::AttachEngine3D
  Height = 3
  Placement = pos=(-20,137,0) rot=(0,0,1;0.785398rad)
  Radius = 3
FEATURE [Part::Compound] Compound974
  Links = -> [Cylinder1941,Cylinder1940]
  Placement = pos=(0,0,25) rot=(0,0,1;0rad)
FEATURE [Part::Box] Box804  label="Krychle804"
  AttacherType = Attacher::AttachEngine3D
  Height = 6
  Length = 68
  Placement = pos=(-34,86,21) rot=(0,0,1;0rad)
  Width = 15
FEATURE [Part::Cut] Cut617
  Base = -> Box804
  Tool = -> Cylinder1937
FEATURE [Part::Cylinder] Cylinder1943  label="Válec1943"
  Angle = 360
  AttacherType = Attacher::AttachEngine3D
  Height = 3
  Placement = pos=(-31,101,0) rot=(0,0,1;0.785398rad)
  Radius = 3
FEATURE [Part::Box] Box803  label="Krychle803"
  AttacherType = Attacher::AttachEngine3D
  Height = 40
  Length = 148
  Placement = pos=(-74,46,16) rot=(0,0,1;0rad)
  Width = 40
FEATURE [Part::Cylinder] Cylinder1935  label="Válec1935"
  Angle = 360
  AttacherType = Attacher::AttachEngine3D
  Height = 6
  Placement = pos=(0,101,21) rot=(0,0,1;0rad)
  Radius = 34
FEATURE [Part::Cut] Cut615
  Base = -> Cylinder1935
  Tool = -> Box803
FEATURE [Part::Cylinder] Cylinder1936  label="Válec1936"
  Angle = 360
  AttacherType = Attacher::AttachEngine3D
  Height = 6
  Placement = pos=(0,83,25) rot=(0,0,1;0rad)
  Radius = 8
FEATURE [Part::Cut] Cut616
  Base = -> Cut615
  Tool = -> Cylinder1936
FEATURE [Part::Chamfer] Chamfer067
  Base = -> Cut616
  Edges = 1 edges r=2: [Edge7]
FEATURE [Part::Cylinder] Cylinder1939  label="Válec1939"
  Angle = 360
  AttacherType = Attacher::AttachEngine3D
  Height = 3
  Placement = pos=(-31,131,0) rot=(0,0,1;0.785398rad)
  Radius = 3
FEATURE [Part::Cylinder] Cylinder1938  label="Válec1938"
  Angle = 360
  AttacherType = Attacher::AttachEngine3D
  Height = 3
  Placement = pos=(31,131,0) rot=(0,0,1;0.785398rad)
  Radius = 3
FEATURE [Part::Compound] Compound975
  Links = -> [Cylinder1939,Cylinder1938]
  Placement = pos=(0,0,25) rot=(0,0,1;0rad)
FEATURE [Part::Cylinder] Cylinder1942  label="Válec1942"
  Angle = 360
  AttacherType = Attacher::AttachEngine3D
  Height = 3
  Placement = pos=(31,101,0) rot=(0,0,1;0.785398rad)
  Radius = 3
FEATURE [Part::Compound] Compound976
  Links = -> [Cylinder1943,Cylinder1942]
  Placement = pos=(0,0,21) rot=(0,0,1;0rad)
FEATURE [Part::Compound] Compound977
  Links = -> [Compound974,Compound975,Compound976]
FEATURE [Part::Cut] Cut618
  Base = -> Cut617
  Tool = -> Compound977
FEATURE [Part::Chamfer] Chamfer068
  Base = -> Cut618
  Edges = 2 edges r=2: [Edge5,Edge25]
FEATURE [Part::Cylinder] Cylinder1961  label="Válec1961"
  Angle = 360
  AttacherType = Attacher::AttachEngine3D
  Height = 3
  Placement = pos=(-31,101,0) rot=(0,0,1;0.785398rad)
  Radius = 3
FEATURE [Part::Cylinder] Cylinder1952  label="Válec1952"
  Angle = 360
  AttacherType = Attacher::AttachEngine3D
  Height = 3
  Placement = pos=(-31,101,0) rot=(0,0,1;0.785398rad)
  Radius = 3
FEATURE [Part::Cylinder] Cylinder1965  label="Válec1965"
  Angle = 360
  AttacherType = Attacher::AttachEngine3D
  Height = 50
  Placement = pos=(-20,137,0) rot=(0,0,1;0.785398rad)
  Radius = 1.5
FEATURE [Part::Cylinder] Cylinder1953  label="Válec1953"
  Angle = 360
  AttacherType = Attacher::AttachEngine3D
  Height = 3
  Placement = pos=(-31,131,0) rot=(0,0,1;0.785398rad)
  Radius = 3
FEATURE [Part::Cylinder] Cylinder1968  label="Válec1968"
  Angle = 360
  AttacherType = Attacher::AttachEngine3D
  Height = 50
  Placement = pos=(-20,137,0) rot=(0,0,1;0.785398rad)
  Radius = 1.5
FEATURE [Part::Cylinder] Cylinder1950  label="Válec1950"
  Angle = 360
  AttacherType = Attacher::AttachEngine3D
  Height = 3
  Placement = pos=(20,137,0) rot=(0,0,1;0.785398rad)
  Radius = 3
FEATURE [Part::Cylinder] Cylinder1958  label="Válec1958"
  Angle = 360
  AttacherType = Attacher::AttachEngine3D
  Height = 3
  Placement = pos=(20,137,0) rot=(0,0,1;0.785398rad)
  Radius = 3
FEATURE [Part::Cylinder] Cylinder1956  label="Válec1956"
  Angle = 360
  AttacherType = Attacher::AttachEngine3D
  Height = 3
  Placement = pos=(31,131,0) rot=(0,0,1;0.785398rad)
  Radius = 3
FEATURE [Part::Cylinder] Cylinder1954  label="Válec1954"
  Angle = 360
  AttacherType = Attacher::AttachEngine3D
  Height = 3
  Placement = pos=(31,131,0) rot=(0,0,1;0.785398rad)
  Radius = 3
FEATURE [Part::Compound] Compound982
  Links = -> [Cylinder1953,Cylinder1954]
  Placement = pos=(0,0,25) rot=(0,0,1;0rad)
FEATURE [Part::Cylinder] Cylinder1957  label="Válec1957"
  Angle = 360
  AttacherType = Attacher::AttachEngine3D
  Height = 3
  Placement = pos=(-31,131,0) rot=(0,0,1;0.785398rad)
  Radius = 3
FEATURE [Part::Compound] Compound987
  Links = -> [Cylinder1957,Cylinder1956]
  Placement = pos=(0,0,25) rot=(0,0,1;0rad)
FEATURE [Part::Cylinder] Cylinder1951  label="Válec1951"
  Angle = 360
  AttacherType = Attacher::AttachEngine3D
  Height = 3
  Placement = pos=(-20,137,0) rot=(0,0,1;0.785398rad)
  Radius = 3
FEATURE [Part::Compound] Compound983
  Links = -> [Cylinder1951,Cylinder1950]
  Placement = pos=(0,0,25) rot=(0,0,1;0rad)
FEATURE [Part::Cylinder] Cylinder1962  label="Válec1962"
  Angle = 360
  AttacherType = Attacher::AttachEngine3D
  Height = 50
  Placement = pos=(-31,131,0) rot=(0,0,1;0.785398rad)
  Radius = 1.5
FEATURE [Part::Cylinder] Cylinder1955  label="Válec1955"
  Angle = 360
  AttacherType = Attacher::AttachEngine3D
  Height = 3
  Placement = pos=(31,101,0) rot=(0,0,1;0.785398rad)
  Radius = 3
FEATURE [Part::Compound] Compound984
  Links = -> [Cylinder1952,Cylinder1955]
  Placement = pos=(0,0,21) rot=(0,0,1;0rad)
FEATURE [Part::Compound] Compound985
  Links = -> [Compound983,Compound982,Compound984]
FEATURE [Part::Cut] Cut619
  Base = -> Chamfer067
  Tool = -> Compound985
FEATURE [Part::Cylinder] Cylinder1959  label="Válec1959"
  Angle = 360
  AttacherType = Attacher::AttachEngine3D
  Height = 3
  Placement = pos=(-20,137,0) rot=(0,0,1;0.785398rad)
  Radius = 3
FEATURE [Part::Compound] Compound986
  Links = -> [Cylinder1959,Cylinder1958]
  Placement = pos=(0,0,25) rot=(0,0,1;0rad)
FEATURE [Part::Cylinder] Cylinder1960  label="Válec1960"
  Angle = 360
  AttacherType = Attacher::AttachEngine3D
  Height = 3
  Placement = pos=(31,101,0) rot=(0,0,1;0.785398rad)
  Radius = 3
FEATURE [Part::Compound] Compound988
  Links = -> [Cylinder1961,Cylinder1960]
  Placement = pos=(0,0,21) rot=(0,0,1;0rad)
FEATURE [Part::Compound] Compound989
  Links = -> [Compound986,Compound987,Compound988]
FEATURE [Part::Cut] Cut620
  Base = -> Cut614
  Tool = -> Compound989
FEATURE [Part::Cut] Cut621
  Base = -> Cut620
  Tool = -> Compound990
FEATURE [Part::Cylinder] Cylinder1963  label="Válec1963"
  Angle = 360
  AttacherType = Attacher::AttachEngine3D
  Height = 50
  Placement = pos=(31,131,0) rot=(0,0,1;0.785398rad)
  Radius = 1.5
FEATURE [Part::Compound] Compound992
  Links = -> [Cylinder1962,Cylinder1963]
FEATURE [Part::Cylinder] Cylinder1964  label="Válec1964"
  Angle = 360
  AttacherType = Attacher::AttachEngine3D
  Height = 50
  Placement = pos=(20,137,0) rot=(0,0,1;0.785398rad)
  Radius = 1.5
FEATURE [Part::Compound] Compound991
  Links = -> [Cylinder1965,Cylinder1964]
FEATURE [Part::Cylinder] Cylinder1966  label="Válec1966"
  Angle = 360
  AttacherType = Attacher::AttachEngine3D
  Height = 50
  Placement = pos=(-31,101,0) rot=(0,0,1;0.785398rad)
  Radius = 1.5
FEATURE [Part::Cylinder] Cylinder1967  label="Válec1967"
  Angle = 360
  AttacherType = Attacher::AttachEngine3D
  Height = 50
  Placement = pos=(31,101,0) rot=(0,0,1;0.785398rad)
  Radius = 1.5
FEATURE [Part::Compound] Compound993
  Links = -> [Cylinder1966,Cylinder1967]
FEATURE [Part::Compound] Compound994
  Links = -> [Compound993,Compound991,Compound992]
FEATURE [Part::Cut] Cut622
  Base = -> Cut619
  Tool = -> Compound994
FEATURE [Part::Cylinder] Cylinder1971  label="Válec1971"
  Angle = 360
  AttacherType = Attacher::AttachEngine3D
  Height = 50
  Placement = pos=(20,137,0) rot=(0,0,1;0.785398rad)
  Radius = 1.5
FEATURE [Part::Compound] Compound997
  Links = -> [Cylinder1968,Cylinder1971]
FEATURE [Part::Cylinder] Cylinder1972  label="Válec1972"
  Angle = 360
  AttacherType = Attacher::AttachEngine3D
  Height = 50
  Placement = pos=(-31,101,0) rot=(0,0,1;0.785398rad)
  Radius = 1.5
FEATURE [Part::Cylinder] Cylinder1974  label="Válec1974"
  Angle = 360
  AttacherType = Attacher::AttachEngine3D
  Height = 6
  Placement = pos=(0,86,16) rot=(0,0,1;0rad)
  Radius = 16
FEATURE [Part::Box] Box805  label="Krychle805"
  AttacherType = Attacher::AttachEngine3D
  Height = 40
  Length = 148
  Placement = pos=(-74,42,16) rot=(0,0,1;0rad)
  Width = 40
FEATURE [Part::Cut] Cut624
  Base = -> Cylinder1974
  Tool = -> Box805
FEATURE [Part::Cylinder] Cylinder1970  label="Válec1970"
  Angle = 360
  AttacherType = Attacher::AttachEngine3D
  Height = 50
  Placement = pos=(31,131,0) rot=(0,0,1;0.785398rad)
  Radius = 1.5
FEATURE [Part::Cylinder] Cylinder1969  label="Válec1969"
  Angle = 360
  AttacherType = Attacher::AttachEngine3D
  Height = 50
  Placement = pos=(-31,131,0) rot=(0,0,1;0.785398rad)
  Radius = 1.5
FEATURE [Part::Compound] Compound998
  Links = -> [Cylinder1969,Cylinder1970]
FEATURE [Part::Cylinder] Cylinder1973  label="Válec1973"
  Angle = 360
  AttacherType = Attacher::AttachEngine3D
  Height = 50
  Placement = pos=(31,101,0) rot=(0,0,1;0.785398rad)
  Radius = 1.5
FEATURE [Part::Compound] Compound995
  Links = -> [Cylinder1972,Cylinder1973]
FEATURE [Part::Compound] Compound996
  Links = -> [Compound995,Compound997,Compound998]
FEATURE [Part::Cut] Cut623
  Base = -> Chamfer068
  Tool = -> Compound996
FEATURE [Part::Chamfer] Chamfer069
  Base = -> Cut624
  Edges = 1 edges r=2: [Edge7]
FEATURE [Part::Compound] Compound999  label="Base_rear-gearbox-cover"
  Links = -> [Tube032,Cut622,Cut623,Cut621,Cut613,Chamfer069]
FEATURE [Mesh::Feature] Mesh001  label="Base_rear-gearbox-cover (Meshed)"
